# Revit family: Workstations-Multi_Level-Teknion-B_ARHB-Run-Off_High_Secondary_Bevel_Base-R2018
name_source: partatom
category: Furniture
revit_build: Autodesk Revit 2018 (Build: 20190510_1515(x64)
units: mm (PartAtom-declared; Revit-internal decimal feet)

## family parameters
Always vertical = Yes
Cut with Voids When Loaded = No
OmniClass Number = 23.40.20.00
OmniClass Title = General Furniture and Specialties
Room Calculation Point = No
Shared = Yes
Work Plane-Based = No

## types (4) — shared parameters
Assembly Code = E2020200
Manufacturer = Teknion
Manufacturer Fax = 416.661.4586
Part Number = B_ARHB
Product Documentation Link = http://www.teknion.com
Product Documentation Link #2 = http://www.teknion.com
Product Documentation Link #3 = http://www.teknion.com
Product Documentation Link #4 = http://www.teknion.com
Product Documentation Link #5 = http://www.teknion.com
Product Line = Expansion Casegoods
Product Page URL = http://www.teknion.com
Series = Expansion Casegoods
Suspended Modesty Panel - Glass Hardware Finish = Paint - Teknion - Mica - Very White
Sustainability Data = http://www.teknion.com
URL = www.teknion.com
Unit Weight URL = http://www.teknion.com
Warranty = http://www.teknion.com

## per-type parameters (varying)
| type | Depth | Description | Model | Worksurface Thickness |
| 1-3/16" Thick WS, 29"d | 29 " | Height-Adjustable Run-Off – High Secondary Desk - Bevel Base, 1-3/16" Thick Worksurface Thickness, Extended Range Electric - 29" to 48", 29" Depth | BMARHBE29_____ | 1.189 " |
| 1-3/16" Thick WS, 35"d | 35 " | Height-Adjustable Run-Off – High Secondary Desk - Bevel Base, 1-3/16" Thick Worksurface Thickness, Extended Range Electric - 29" to 48", 35" Depth | BMARHBE35_____ | 1.189 " |
| 1-9/16" Thick WS, 35"d | 35 " | Height-Adjustable Run-Off – High Secondary Desk - Bevel Base, 1-9/16" Thick Worksurface Thickness, Extended Range Electric - 29" to 48", 35" Depth | BXARHBE35_____ | 1.555 " |
| 1-9/16" Thick WS, 29"d | 29 " | Height-Adjustable Run-Off – High Secondary Desk - Bevel Base, 1-9/16" Thick Worksurface Thickness, Extended Range Electric - 29" to 48", 29" Depth | BXARHBE29_____ | 1.555 " |

## geometry (parser evidence)
native form markers: Blend x1, Sweep x4
no freeform markers — native parametric forms only
